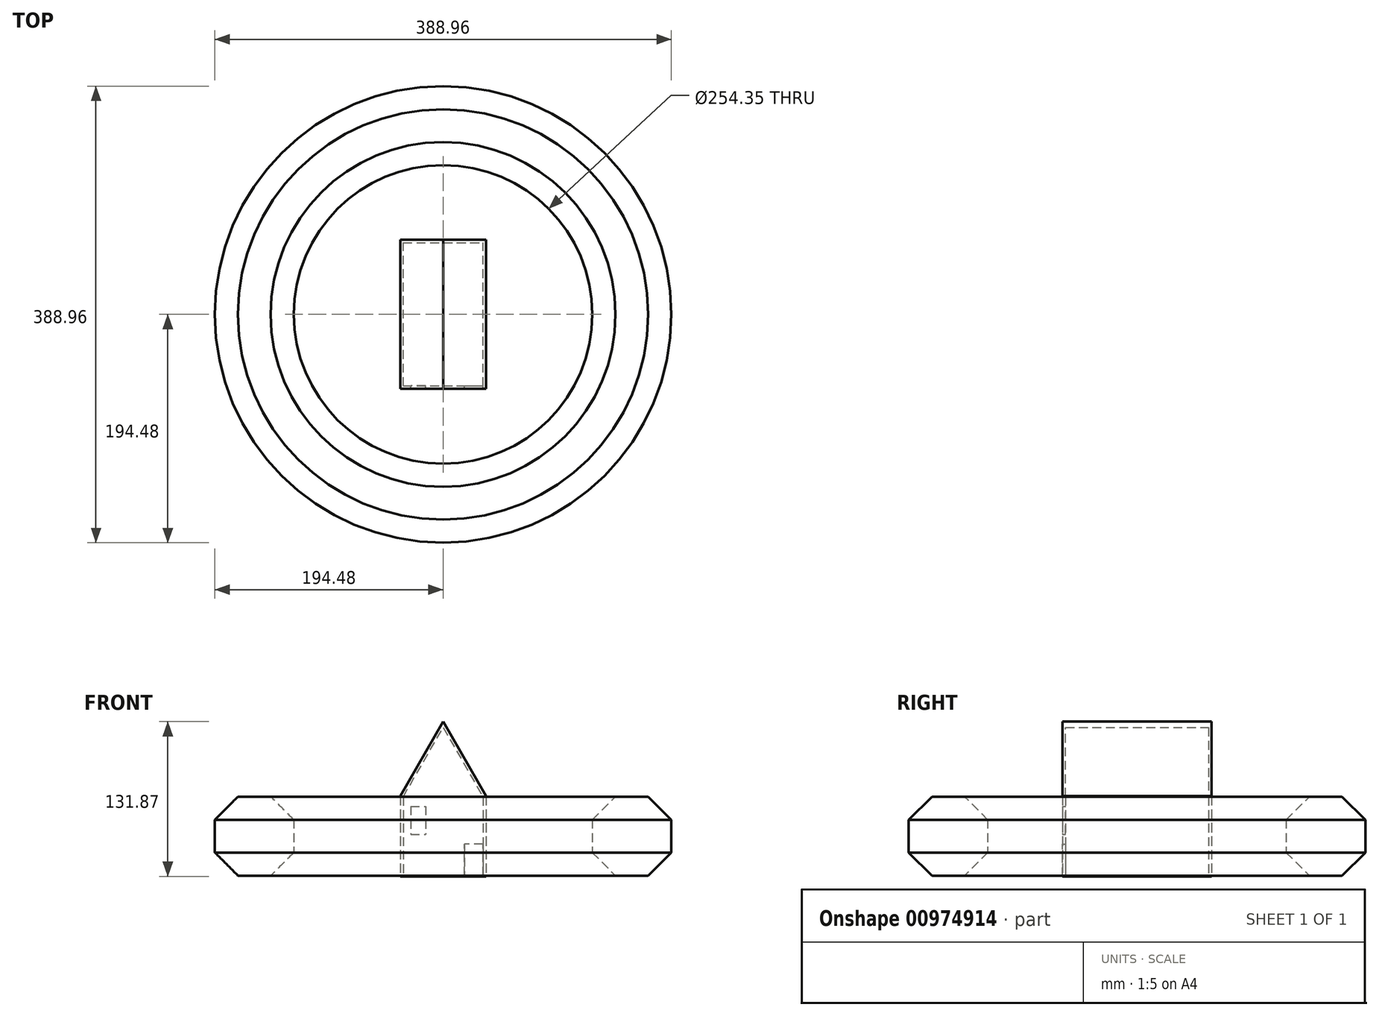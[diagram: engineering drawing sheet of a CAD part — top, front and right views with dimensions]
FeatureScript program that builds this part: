
annotation { "Feature Type Name" : "Feature", "Feature Type Description" : "" }
export const myFeature = defineFeature(function(context is Context, id is Id, definition is map)
    precondition{}
    {
        {
            var Q0;
            Q0=qCreatedBy(makeId("Front.planeOp"),FACE);
            var sketch = newSketch(context, id + "F0", { "sketchPlane" : qUnion([Q0])});
            skLineSegment(sketch, "E0.top", {"start": v(-36.57, -34.27) * mm, "end": v(36.57, -34.27) * mm});
            skLineSegment(sketch, "E0.left", {"start": v(-36.57, 34.27) * mm, "end": v(-36.57, -34.27) * mm});
            skLineSegment(sketch, "E0.right", {"start": v(36.57, 34.27) * mm, "end": v(36.57, -34.27) * mm});
            skPoint(sketch, "E0.middle", {"position": v(0, 0) * mm});
            skLineSegment(sketch, "E1.bottom", {"start": v(-27.58, 25.4) * mm, "end": v(-14.82, 25.4) * mm});
            skLineSegment(sketch, "E1.top", {"start": v(-27.58, 1.58) * mm, "end": v(-14.82, 1.58) * mm});
            skLineSegment(sketch, "E1.left", {"start": v(-27.58, 25.4) * mm, "end": v(-27.58, 1.58) * mm});
            skLineSegment(sketch, "E1.right", {"start": v(-14.82, 25.4) * mm, "end": v(-14.82, 1.58) * mm});
            skPoint(sketch, "E1.middle", {"position": v(-21.2, 13.49) * mm});
            skLineSegment(sketch, "E2.bottom", {"start": v(33.96, -34.27) * mm, "end": v(18.22, -34.27) * mm});
            skLineSegment(sketch, "E2.top", {"start": v(33.96, -6.87) * mm, "end": v(18.22, -6.87) * mm});
            skLineSegment(sketch, "E2.left", {"start": v(33.96, -34.27) * mm, "end": v(33.96, -6.87) * mm});
            skLineSegment(sketch, "E2.right", {"start": v(18.22, -34.27) * mm, "end": v(18.22, -6.87) * mm});
            skLineSegment(sketch, "E3", {"start": v(-36.57, 34.27) * mm, "end": v(0, 97.6) * mm});
            skLineSegment(sketch, "E4", {"start": v(0, 97.6) * mm, "end": v(36.57, 34.27) * mm});
            skSolve(sketch);
        }
        {
            var Q0;
            {var subQ1=sQuery(id+"F0.wireOp",EDGE,"E0.left");Q0=makeQuery(id+"F0.imprint","IMPRINT",FACE,{"disambiguationData":[TD([[makeQuery(id+"F0.imprint","IMPRINT",EDGE,{"derivedFrom":subQ1}),1.0]])]});}
            var Q1;
            Q1=makeQuery(id+"F0.imprint","IMPRINT",FACE,{"disambiguationData":[TD([[makeQuery(id+"F0.imprint","IMPRINT",EDGE,{"derivedFrom":sQuery(id+"F0.wireOp",EDGE,"E2.top")}),1.0]])]});
            var Q2;
            Q2=makeQuery(id+"F0.imprint","IMPRINT",FACE,{"disambiguationData":[TD([[makeQuery(id+"F0.imprint","IMPRINT",EDGE,{"derivedFrom":sQuery(id+"F0.wireOp",EDGE,"E1.bottom")}),-1.0]])]});
            extrude(context, id + "F1", {"entities" : qUnion([Q0, Q1, Q2]), "endBound" : BoundingType.SYMMETRIC, "depth" : 127 * mm, "offsetDistance" : 25.4 * mm});
        }
        {
            var Q0;
            Q0=makeQuery(id+"F1.opExtrude","SWEPT_FACE",FACE,{"disambiguationData":[OSD([sQuery(id+"F0.wireOp",EDGE,"E0.top")])]});
            shell(context, id + "F2", {"entities" : qUnion([Q0]), "thickness" : 2.54 * mm});
        }
        {
            var Q0;
            Q0=makeQuery(id+"F0.imprint","IMPRINT",FACE,{"disambiguationData":[TD([[makeQuery(id+"F0.imprint","IMPRINT",EDGE,{"derivedFrom":sQuery(id+"F0.wireOp",EDGE,"E1.bottom")}),-1.0]])]});
            var Q1;
            Q1=makeQuery(id+"F0.imprint","IMPRINT",FACE,{"disambiguationData":[TD([[makeQuery(id+"F0.imprint","IMPRINT",EDGE,{"derivedFrom":sQuery(id+"F0.wireOp",EDGE,"E2.top")}),1.0]])]});
            var Q2;
            Q2=makeQuery(id+"F1.opExtrude","CAP_FACE",FACE,{"disambiguationData":[OSD([sQuery(id+"F0.wireOp",EDGE,"E0.top"),sQuery(id+"F0.wireOp",EDGE,"E0.left"),sQuery(id+"F0.wireOp",EDGE,"E0.right"),sQuery(id+"F0.wireOp",EDGE,"E3"),sQuery(id+"F0.wireOp",EDGE,"E4")])],"isStart":false});
            extrude(context, id + "F3", {"entities" : qUnion([Q0, Q1]), "operationType" : NewBodyOperationType.REMOVE, "endBound" : BoundingType.UP_TO_SURFACE, "depth" : 127 * mm, "endBoundEntityFace" : qUnion([Q2]), "offsetDistance" : 25.4 * mm});
        }
        {
            var Q0;
            Q0=qCreatedBy(makeId("Front.planeOp"),FACE);
            var sketch = newSketch(context, id + "F4", { "sketchPlane" : qUnion([Q0])});
            skCircle(sketch, "E5.cCircle", {"center": v(-160.83, 0) * mm, "radius": 33.65 * mm, "construction": true});
            skLineSegment(sketch, "E5.0", {"start": v(-127.17, -13.94) * mm, "end": v(-146.89, -33.65) * mm});
            skLineSegment(sketch, "E5.1", {"start": v(-146.89, -33.65) * mm, "end": v(-174.77, -33.65) * mm});
            skLineSegment(sketch, "E5.2", {"start": v(-174.77, -33.65) * mm, "end": v(-194.48, -13.94) * mm});
            skLineSegment(sketch, "E5.3", {"start": v(-194.48, -13.94) * mm, "end": v(-194.48, 13.94) * mm});
            skLineSegment(sketch, "E5.4", {"start": v(-194.48, 13.94) * mm, "end": v(-174.77, 33.65) * mm});
            skLineSegment(sketch, "E5.5", {"start": v(-174.77, 33.65) * mm, "end": v(-146.89, 33.65) * mm});
            skLineSegment(sketch, "E5.6", {"start": v(-146.89, 33.65) * mm, "end": v(-127.17, 13.94) * mm});
            skLineSegment(sketch, "E5.7", {"start": v(-127.17, 13.94) * mm, "end": v(-127.17, -13.94) * mm});
            skPoint(sketch, "E5.0.midPoint", {"position": v(-137.03, -23.8) * mm});
            skLineSegment(sketch, "E6", {"start": v(0, 0) * mm, "end": v(0, 97.95) * mm, "construction": true});
            skSolve(sketch);
        }
        {
            var Q0;
            Q0=makeQuery(id+"F4.imprint","IMPRINT",FACE,{"disambiguationData":[TD([[makeQuery(id+"F4.imprint","IMPRINT",EDGE,{"derivedFrom":sQuery(id+"F4.wireOp",EDGE,"E5.0")}),-1.0]])]});
            var Q1;
            Q1=sQuery(id+"F4.wireOp",EDGE,"E6");
            revolve(context, id + "F5", {"surfaceOperationType" : NewSurfaceOperationType.NEW, "entities" : qUnion([Q0]), "axis" : qUnion([Q1]), "revolveType" : RevolveType.FULL});
        }
    });
